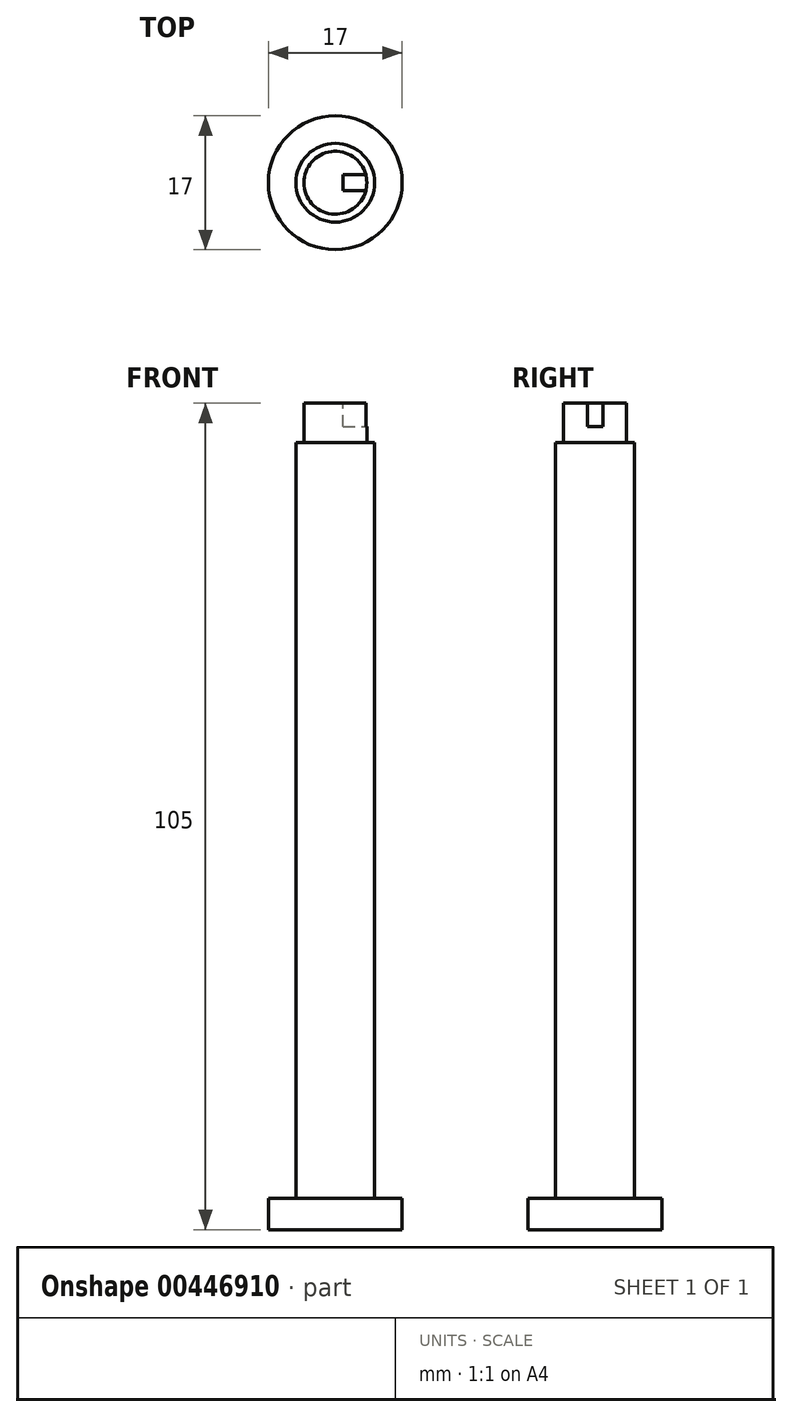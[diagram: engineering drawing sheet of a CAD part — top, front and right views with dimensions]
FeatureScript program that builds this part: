
annotation { "Feature Type Name" : "Feature", "Feature Type Description" : "" }
export const myFeature = defineFeature(function(context is Context, id is Id, definition is map)
    precondition{}
    {
        {
            var Q0;
            Q0=qCreatedBy(makeId("Top.planeOp"),FACE);
            var sketch = newSketch(context, id + "F0", { "sketchPlane" : qUnion([Q0])});
            skCircle(sketch, "E0", {"center": v(0, 0) * mm, "radius": 8.5 * mm});
            skSolve(sketch);
        }
        {
            var Q0;
            Q0=qSketchRegion(id+"F0",true);
            extrude(context, id + "F1", {"entities" : qUnion([Q0]), "depth" : 4 * mm});
        }
        {
            var Q0;
            Q0=qCreatedBy(makeId("Top.planeOp"),FACE);
            cPlane(context, id + "F2", {"entities" : qUnion([Q0]), "cplaneType" : CPlaneType.OFFSET, "offset" : 4 * mm, "width" : 150 * mm, "height" : 150 * mm});
        }
        {
            var Q0;
            Q0=qCreatedBy(makeId("Top.planeOp"),FACE);
            var sketch = newSketch(context, id + "F3", { "sketchPlane" : qUnion([Q0])});
            skCircle(sketch, "E1", {"center": v(0, 0) * mm, "radius": 5 * mm});
            skSolve(sketch);
        }
        {
            var Q0;
            Q0=qSketchRegion(id+"F3",true);
            extrude(context, id + "F4", {"entities" : qUnion([Q0]), "operationType" : NewBodyOperationType.ADD, "depth" : 100 * mm});
        }
        {
            var Q0;
            Q0=qCreatedBy(makeId("Right.planeOp"),FACE);
            var sketch = newSketch(context, id + "F5", { "sketchPlane" : qUnion([Q0])});
            skLineSegment(sketch, "E2.bottom", {"start": v(0, 105) * mm, "end": v(4, 105) * mm});
            skLineSegment(sketch, "E2.top", {"start": v(0, 100) * mm, "end": v(4, 100) * mm});
            skLineSegment(sketch, "E2.left", {"start": v(0, 105) * mm, "end": v(0, 100) * mm});
            skLineSegment(sketch, "E2.right", {"start": v(4, 105) * mm, "end": v(4, 100) * mm});
            skSolve(sketch);
        }
        {
            var Q0;
            Q0=makeQuery(id+"F5.imprint","IMPRINT",FACE,{"disambiguationData":[TD([[makeQuery(id+"F5.imprint","IMPRINT",EDGE,{"derivedFrom":sQuery(id+"F5.wireOp",EDGE,"E2.bottom")}),-1.0]])]});
            var Q1;
            Q1=sQuery(id+"F5.wireOp",EDGE,"E2.left");
            revolve(context, id + "F6", {"operationType" : NewBodyOperationType.ADD, "entities" : qUnion([Q0]), "axis" : qUnion([Q1]), "revolveType" : RevolveType.FULL});
        }
        {
            var Q0;
            Q0=qCreatedBy(id+"F2.planeOp",FACE);
            var sketch = newSketch(context, id + "F7", { "sketchPlane" : qUnion([Q0])});
            skLineSegment(sketch, "E3", {"start": v(8.44, 1) * mm, "end": v(8.44, -1) * mm});
            skSolve(sketch);
        }
        {
            var Q0;
            Q0=makeQuery(id+"F6.opRevolve","SWEPT_FACE",FACE,{"disambiguationData":[OSD([sQuery(id+"F5.wireOp",EDGE,"E2.bottom")])]});
            var sketch = newSketch(context, id + "F8", { "sketchPlane" : qUnion([Q0])});
            skLineSegment(sketch, "E4.bottom", {"start": v(1, 1) * mm, "end": v(5.75, 1) * mm});
            skLineSegment(sketch, "E4.top", {"start": v(1, -1) * mm, "end": v(5.75, -1) * mm});
            skLineSegment(sketch, "E4.left", {"start": v(1, 1) * mm, "end": v(1, -1) * mm});
            skLineSegment(sketch, "E4.right", {"start": v(5.75, 1) * mm, "end": v(5.75, -1) * mm});
            skSolve(sketch);
        }
        {
            var Q0;
            {var subQ0=sQuery(id+"F8.wireOp",EDGE,"E4.left");Q0=makeQuery(id+"F8.imprint","IMPRINT",FACE,{"disambiguationData":[TD([[makeQuery(id+"F8.imprint","IMPRINT",EDGE,{"derivedFrom":subQ0}),1.0]])]});}
            extrude(context, id + "F9", {"entities" : qUnion([Q0]), "operationType" : NewBodyOperationType.REMOVE, "oppositeDirection" : true, "depth" : 3 * mm});
        }
    });
